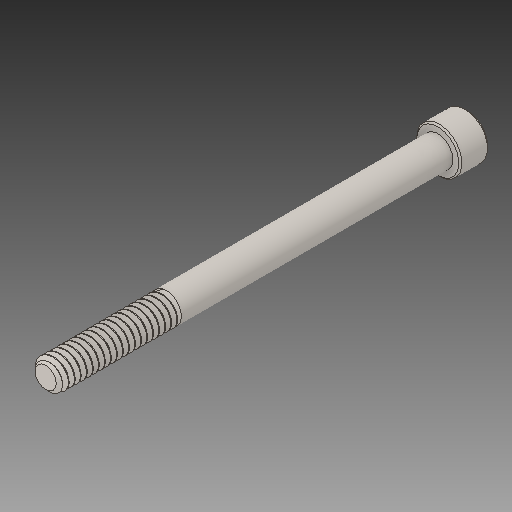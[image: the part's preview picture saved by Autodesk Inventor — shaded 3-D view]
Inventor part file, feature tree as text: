
AUTODESK INVENTOR PART (.ipt)
format: ipt  version: 2017 (Build 210142000, 142)  size: 637,440 bytes
history: native  units: in
note: dims shown in document units (in); Inventor stores cm internally (conversion verified against a paired STEP export)
features: chamfer x1
ambient origin geometry x8: Origin, YZ Plane, XZ Plane, XY Plane, X Axis, Y Axis, Z Axis, Center Point
bodies: Solid1 (feature_tree)
feature tree (1):
  chamfer  "Chamfer2"  [1 undecoded]
note: 1 required parameter value undecoded (feature->parameter linkage not recoverable at this tier; creation-order binding heuristic only, values carry confidence <= 0.55)
